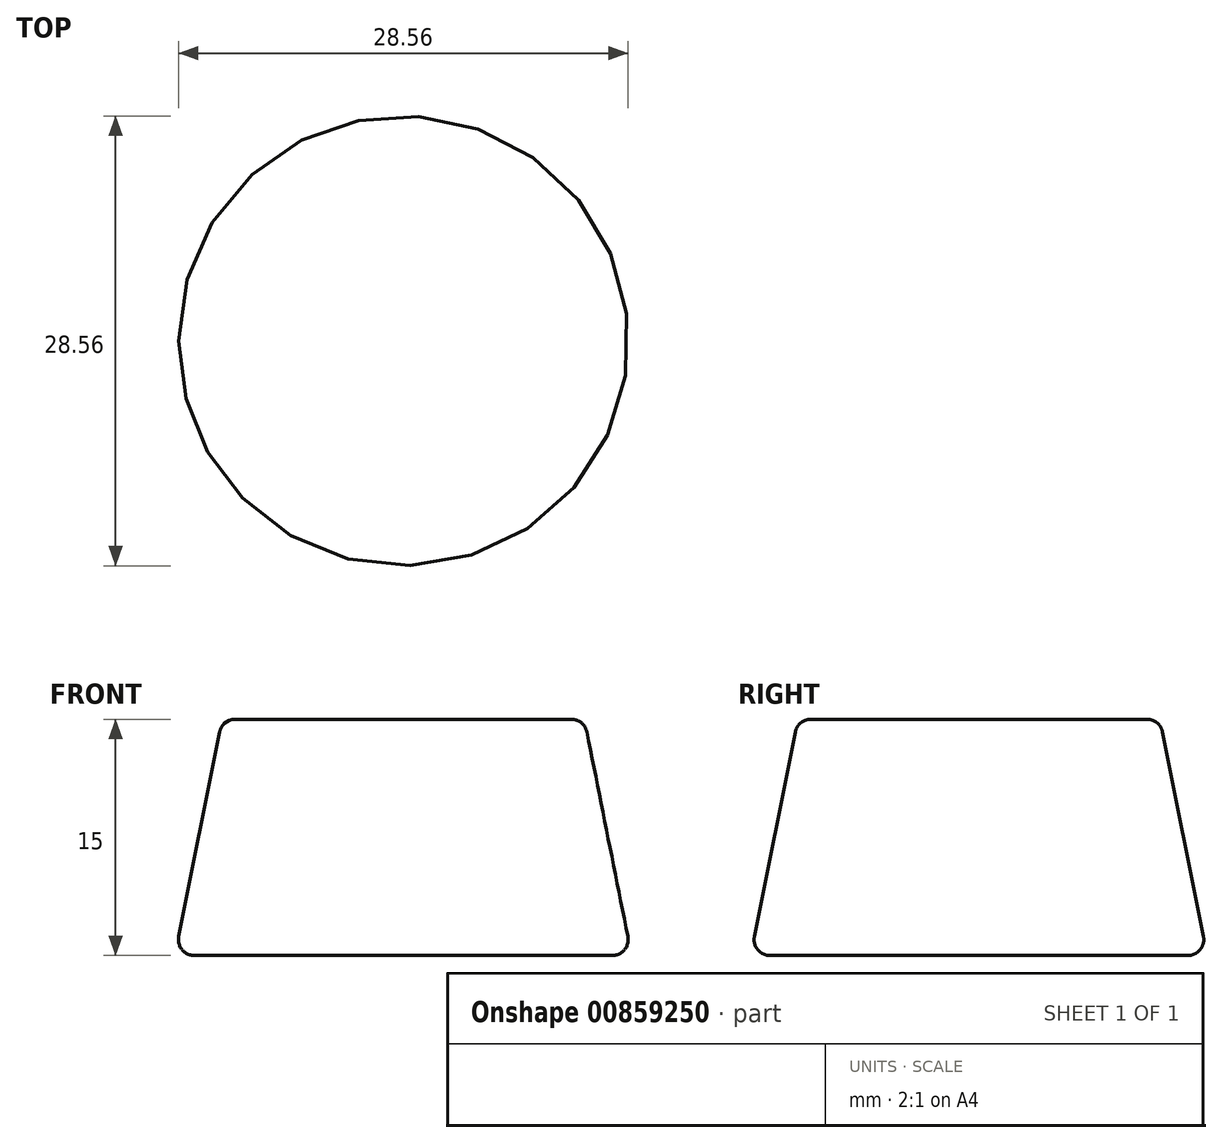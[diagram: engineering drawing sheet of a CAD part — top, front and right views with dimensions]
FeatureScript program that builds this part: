
annotation { "Feature Type Name" : "Feature", "Feature Type Description" : "" }
export const myFeature = defineFeature(function(context is Context, id is Id, definition is map)
    precondition{}
    {
        {
            var Q0;
            Q0=qCreatedBy(makeId("Front.planeOp"),FACE);
            var sketch = newSketch(context, id + "F0", { "sketchPlane" : qUnion([Q0])});
            skLineSegment(sketch, "E0", {"start": v(0, 15) * mm, "end": v(0, 0) * mm});
            skLineSegment(sketch, "E1", {"start": v(0, 15) * mm, "end": v(11.5, 15) * mm});
            skLineSegment(sketch, "E2", {"start": v(11.5, 15) * mm, "end": v(14.5, 0) * mm});
            skLineSegment(sketch, "E3", {"start": v(14.5, 0) * mm, "end": v(0, 0) * mm});
            skSolve(sketch);
        }
        {
            var Q0;
            Q0=makeQuery(id+"F0.imprint","IMPRINT",FACE,{"disambiguationData":[TD([[makeQuery(id+"F0.imprint","IMPRINT",EDGE,{"derivedFrom":sQuery(id+"F0.wireOp",EDGE,"E0")}),1.0]])]});
            var Q1;
            Q1=sQuery(id+"F0.wireOp",EDGE,"E0");
            revolve(context, id + "F1", {"surfaceOperationType" : NewSurfaceOperationType.NEW, "entities" : qUnion([Q0]), "axis" : qUnion([Q1]), "revolveType" : RevolveType.FULL});
        }
        {
            var Q0;
            Q0=makeQuery(id+"F1.opRevolve","SWEPT_EDGE",EDGE,{"disambiguationData":[OSD([sQuery(id+"F0.wireOp",EDGE,"E1"),sQuery(id+"F0.wireOp",EDGE,"E2")])]});
            var Q1;
            Q1=makeQuery(id+"F1.opRevolve","SWEPT_EDGE",EDGE,{"disambiguationData":[OSD([sQuery(id+"F0.wireOp",EDGE,"E2"),sQuery(id+"F0.wireOp",EDGE,"E3")])]});
            fillet(context, id + "F2", {"entities" : qUnion([Q0, Q1]), "radius" : 1 * mm, "tangentPropagation" : true, "allowEdgeOverflow" : false});
        }
    });
